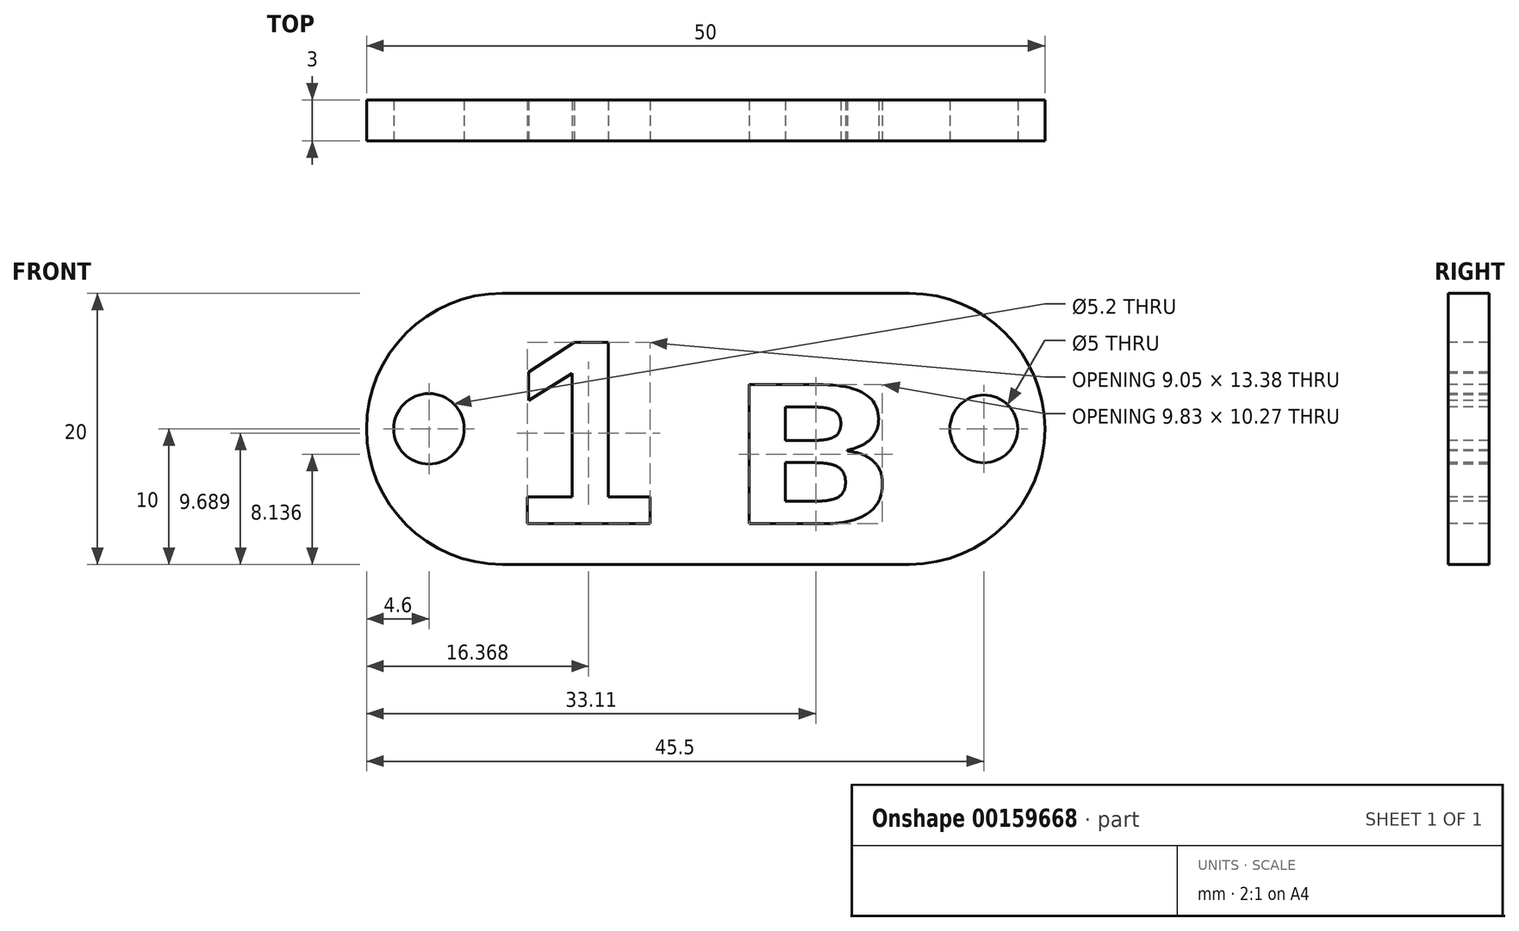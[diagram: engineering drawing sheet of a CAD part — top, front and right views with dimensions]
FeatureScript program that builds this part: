
annotation { "Feature Type Name" : "Feature", "Feature Type Description" : "" }
export const myFeature = defineFeature(function(context is Context, id is Id, definition is map)
    precondition{}
    {
        {
            var Q0;
            Q0=qCreatedBy(makeId("Front.planeOp"),FACE);
            var sketch = newSketch(context, id + "F0", { "sketchPlane" : qUnion([Q0])});
            skLineSegment(sketch, "E0.bottom", {"start": v(25, 10) * mm, "end": v(-25, 10) * mm});
            skLineSegment(sketch, "E0.top", {"start": v(25, -10) * mm, "end": v(-25, -10) * mm});
            skLineSegment(sketch, "E0.left", {"start": v(25, 10) * mm, "end": v(25, -10) * mm});
            skLineSegment(sketch, "E0.right", {"start": v(-25, 10) * mm, "end": v(-25, -10) * mm});
            skPoint(sketch, "E0.middle", {"position": v(0, 0) * mm});
            skSolve(sketch);
        }
        {
            var Q0;
            Q0=makeQuery(id+"F0.imprint","IMPRINT",FACE,{"disambiguationData":[TD([[makeQuery(id+"F0.imprint","IMPRINT",EDGE,{"derivedFrom":sQuery(id+"F0.wireOp",EDGE,"E0.bottom")}),1.0]])]});
            extrude(context, id + "F1", {"entities" : qUnion([Q0]), "depth" : 3 * mm});
        }
        {
            var Q0;
            Q0=makeQuery(id+"F1.opExtrude","CAP_FACE",FACE,{"disambiguationData":[OSD([sQuery(id+"F0.wireOp",EDGE,"E0.bottom"),sQuery(id+"F0.wireOp",EDGE,"E0.top"),sQuery(id+"F0.wireOp",EDGE,"E0.left"),sQuery(id+"F0.wireOp",EDGE,"E0.right")])],"isStart":false});
            var sketch = newSketch(context, id + "F2", { "sketchPlane" : qUnion([Q0])});
            skText(sketch, "E1", { "text": "1 в", "fontName": "Arimo-Bold.ttf"});
            skLineSegment(sketch, "E2", {"start": v(-14.38, 0) * mm, "end": v(14.38, 0) * mm, "construction": true});
            skPoint(sketch, "E3", {"position": v(0, 0) * mm});
            skCircle(sketch, "E4", {"center": v(20.5, 0) * mm, "radius": 2.5 * mm});
            skCircle(sketch, "E5", {"center": v(-20.4, 0) * mm, "radius": 2.6 * mm});
            const initialGuessF2  = {"E1": [-0.01438, -0.007, 1, 0, 0.014]};
            skSetInitialGuess(sketch, initialGuessF2);
            skSolve(sketch);
        }
        {
            var Q0;
            Q0=qSketchRegion(id+"F2",true);
            extrude(context, id + "F3", {"entities" : qUnion([Q0]), "operationType" : NewBodyOperationType.REMOVE, "endBound" : BoundingType.THROUGH_ALL, "oppositeDirection" : true, "depth" : 25 * mm});
        }
        {
            var Q0;
            Q0=makeQuery(id+"F1.opExtrude","SWEPT_EDGE",EDGE,{"disambiguationData":[OSD([sQuery(id+"F0.wireOp",EDGE,"E0.bottom"),sQuery(id+"F0.wireOp",EDGE,"E0.right")])]});
            var Q1;
            Q1=makeQuery(id+"F1.opExtrude","SWEPT_EDGE",EDGE,{"disambiguationData":[OSD([sQuery(id+"F0.wireOp",EDGE,"E0.top"),sQuery(id+"F0.wireOp",EDGE,"E0.right")])]});
            var Q2;
            Q2=makeQuery(id+"F1.opExtrude","SWEPT_EDGE",EDGE,{"disambiguationData":[OSD([sQuery(id+"F0.wireOp",EDGE,"E0.bottom"),sQuery(id+"F0.wireOp",EDGE,"E0.left")])]});
            var Q3;
            Q3=makeQuery(id+"F1.opExtrude","SWEPT_EDGE",EDGE,{"disambiguationData":[OSD([sQuery(id+"F0.wireOp",EDGE,"E0.top"),sQuery(id+"F0.wireOp",EDGE,"E0.left")])]});
            fillet(context, id + "F4", {"entities" : qUnion([Q0, Q1, Q2, Q3]), "radius" : 10 * mm, "tangentPropagation" : true, "allowEdgeOverflow" : false});
        }
    });
